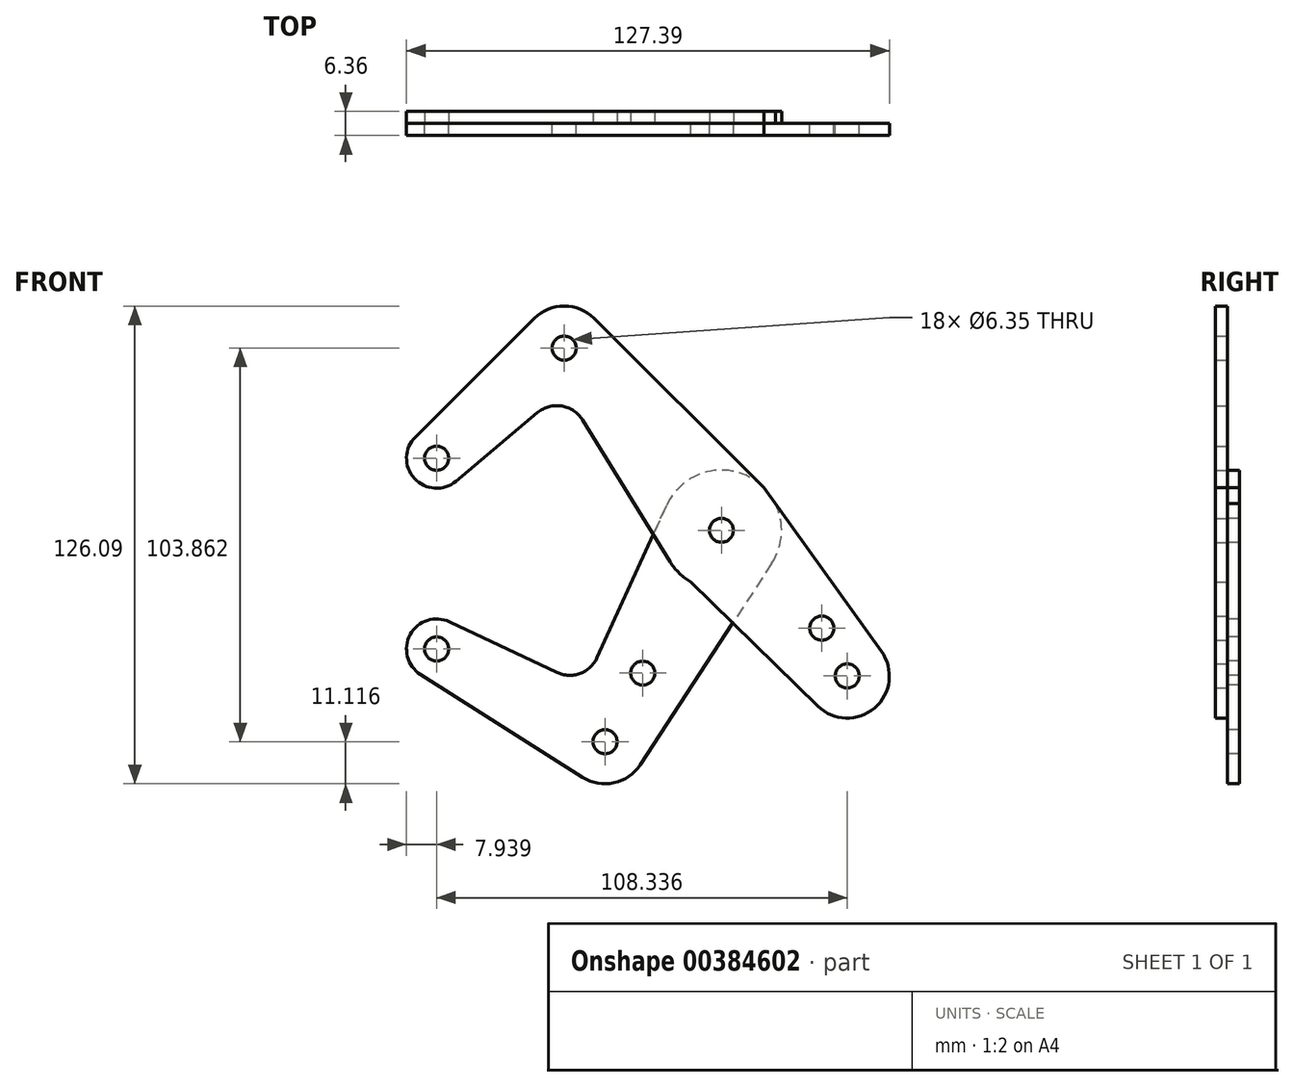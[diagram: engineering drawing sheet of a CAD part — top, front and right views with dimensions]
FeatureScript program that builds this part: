
annotation { "Feature Type Name" : "Feature", "Feature Type Description" : "" }
export const myFeature = defineFeature(function(context is Context, id is Id, definition is map)
    precondition{}
    {
        {
            var Q0;
            Q0=qCreatedBy(makeId("Front.planeOp"),FACE);
            var sketch = newSketch(context, id + "F0", { "sketchPlane" : qUnion([Q0])});
            skCircle(sketch, "E0", {"center": v(0, 0) * mm, "radius": 15.88 * mm});
            skCircle(sketch, "E1", {"center": v(-41.5, 48.07) * mm, "radius": 11.11 * mm});
            skCircle(sketch, "E2", {"center": v(33.2, -38.45) * mm, "radius": 11.11 * mm});
            skCircle(sketch, "E3", {"center": v(-75.14, 19.02) * mm, "radius": 7.94 * mm});
            skLineSegment(sketch, "E4", {"start": v(-80.74, 24.65) * mm, "end": v(-49.34, 55.94) * mm});
            skLineSegment(sketch, "E5", {"start": v(-33.65, 55.94) * mm, "end": v(11.2, 11.25) * mm});
            skLineSegment(sketch, "E6", {"start": v(11.2, 11.25) * mm, "end": v(42.22, -31.98) * mm});
            skLineSegment(sketch, "E7", {"start": v(-70.03, 12.95) * mm, "end": v(-48.54, 31.03) * mm});
            skLineSegment(sketch, "E8", {"start": v(-36.66, 29.13) * mm, "end": v(-13.5, -8.34) * mm});
            skLineSegment(sketch, "E9", {"start": v(-13.5, -8.34) * mm, "end": v(25.43, -46.4) * mm});
            skPoint(sketch, "E10.visualSharp", {"position": v(-41.5, 36.96) * mm});
            skArc(sketch, "E10.filletArc", {"start": v(-36.66, 29.13) * mm, "mid": v(-42.16, 32.8) * mm, "end": v(-48.54, 31.03) * mm});
            skCircle(sketch, "E11", {"center": v(33.2, -38.45) * mm, "radius": 3.18 * mm});
            skCircle(sketch, "E12", {"center": v(0, 0) * mm, "radius": 3.18 * mm});
            skCircle(sketch, "E13", {"center": v(-41.5, 48.07) * mm, "radius": 3.18 * mm});
            skCircle(sketch, "E14", {"center": v(-75.14, 19.02) * mm, "radius": 3.18 * mm});
            skLineSegment(sketch, "E15", {"start": v(-41.5, 48.07) * mm, "end": v(33.2, -38.45) * mm, "construction": true});
            skLineSegment(sketch, "E16", {"start": v(-75.14, 19.02) * mm, "end": v(-41.5, 48.07) * mm, "construction": true});
            skCircle(sketch, "E17", {"center": v(26.5, -25.83) * mm, "radius": 3.18 * mm});
            skCircle(sketch, "E18", {"center": v(0, 0) * mm, "radius": 3.98 * mm});
            skCircle(sketch, "E19", {"center": v(-30.7, -55.8) * mm, "radius": 11.11 * mm});
            skCircle(sketch, "E20", {"center": v(-20.74, -37.7) * mm, "radius": 3.18 * mm});
            skLineSegment(sketch, "E21", {"start": v(0, 0) * mm, "end": v(-30.7, -55.8) * mm, "construction": true});
            skLineSegment(sketch, "E22", {"start": v(13.3, -8.67) * mm, "end": v(-21.38, -61.86) * mm});
            skLineSegment(sketch, "E23", {"start": v(-32.8, -33.63) * mm, "end": v(-14.44, 6.59) * mm});
            skCircle(sketch, "E24", {"center": v(-75.14, -31.34) * mm, "radius": 7.94 * mm});
            skLineSegment(sketch, "E25", {"start": v(-75.14, 19.02) * mm, "end": v(-75.14, -31.34) * mm, "construction": true});
            skLineSegment(sketch, "E26", {"start": v(-71.76, -24.16) * mm, "end": v(-43.41, -37.52) * mm});
            skLineSegment(sketch, "E27", {"start": v(-79.4, -38.04) * mm, "end": v(-36.65, -65.18) * mm});
            skLineSegment(sketch, "E28", {"start": v(-75.14, -31.34) * mm, "end": v(-30.7, -55.8) * mm, "construction": true});
            skPoint(sketch, "E29.visualSharp", {"position": v(-36.13, -40.95) * mm});
            skArc(sketch, "E29.filletArc", {"start": v(-43.41, -37.52) * mm, "mid": v(-37.29, -37.79) * mm, "end": v(-32.8, -33.63) * mm});
            skCircle(sketch, "E30", {"center": v(-75.14, -31.34) * mm, "radius": 3.18 * mm});
            skCircle(sketch, "E31", {"center": v(-30.7, -55.8) * mm, "radius": 3.18 * mm});
            skSolve(sketch);
        }
        {
            var Q0;
            {var subQ0=sQuery(id+"F0.wireOp",EDGE,"E4");Q0=makeQuery(id+"F0.imprint","IMPRINT",FACE,{"disambiguationData":[TD([[makeQuery(id+"F0.imprint","IMPRINT",EDGE,{"derivedFrom":subQ0}),-1.0]])]});}
            var Q1;
            Q1=makeQuery(id+"F0.imprint","IMPRINT",FACE,{"disambiguationData":[TD([[makeQuery(id+"F0.imprint","IMPRINT",EDGE,{"derivedFrom":sQuery(id+"F0.wireOp",EDGE,"E18")}),-1.0]])]});
            var Q2;
            Q2=makeQuery(id+"F0.imprint","IMPRINT",FACE,{"disambiguationData":[TD([[makeQuery(id+"F0.imprint","IMPRINT",EDGE,{"derivedFrom":sQuery(id+"F0.wireOp",EDGE,"E13")}),-1.0]])]});
            var Q3;
            Q3=makeQuery(id+"F0.imprint","IMPRINT",FACE,{"disambiguationData":[TD([[makeQuery(id+"F0.imprint","IMPRINT",EDGE,{"derivedFrom":sQuery(id+"F0.wireOp",EDGE,"E14")}),-1.0]])]});
            var Q4;
            Q4=makeQuery(id+"F0.imprint","IMPRINT",FACE,{"disambiguationData":[TD([[makeQuery(id+"F0.imprint","IMPRINT",EDGE,{"derivedFrom":sQuery(id+"F0.wireOp",EDGE,"E12")}),-1.0]])]});
            var Q5;
            {var subQ1=sQuery(id+"F0.wireOp",EDGE,"E0");var subQ3=sQuery(id+"F0.wireOp",EDGE,"E23");var subQ4=makeQuery(id+"F0.imprint","INTERSECT",VERTEX,{"derivedFrom":[subQ1,subQ3]});Q5=makeQuery(id+"F0.imprint","IMPRINT",FACE,{"disambiguationData":[TD([[makeQuery(id+"F0.imprint","IMPRINT",EDGE,{"disambiguationData":[TD([[subQ4,1.0]])],"derivedFrom":subQ3}),-1.0]])]});}
            var Q6;
            {var subQ0=sQuery(id+"F0.wireOp",EDGE,"E22");var subQ1=sQuery(id+"F0.wireOp",EDGE,"E0");var subQ2=makeQuery(id+"F0.imprint","INTERSECT",VERTEX,{"derivedFrom":[subQ1,subQ0]});Q6=makeQuery(id+"F0.imprint","IMPRINT",FACE,{"disambiguationData":[TD([[makeQuery(id+"F0.imprint","IMPRINT",EDGE,{"disambiguationData":[TD([[subQ2,1.0]])],"derivedFrom":subQ1}),-1.0]])]});}
            var Q7;
            {var subQ9=sQuery(id+"F0.wireOp",EDGE,"E17");Q7=makeQuery(id+"F0.imprint","IMPRINT",FACE,{"disambiguationData":[TD([[makeQuery(id+"F0.imprint","IMPRINT",EDGE,{"derivedFrom":subQ9}),-1.0]])]});}
            var Q8;
            Q8=makeQuery(id+"F0.imprint","IMPRINT",FACE,{"disambiguationData":[TD([[makeQuery(id+"F0.imprint","IMPRINT",EDGE,{"derivedFrom":sQuery(id+"F0.wireOp",EDGE,"E11")}),-1.0]])]});
            var Q9;
            {var subQ0=sQuery(id+"F0.wireOp",EDGE,"E9");var subQ1=sQuery(id+"F0.wireOp",EDGE,"E0");var subQ3=makeQuery(id+"F0.imprint","INTERSECT",VERTEX,{"derivedFrom":[subQ1,subQ0]});Q9=makeQuery(id+"F0.imprint","IMPRINT",FACE,{"disambiguationData":[TD([[makeQuery(id+"F0.imprint","IMPRINT",EDGE,{"disambiguationData":[TD([[subQ3,1.0]])],"derivedFrom":subQ1}),1.0]])]});}
            extrude(context, id + "F1", {"entities" : qUnion([Q0, Q1, Q2, Q3, Q4, Q5, Q6, Q7, Q8, Q9]), "depth" : 3.17 * mm});
        }
        {
            var Q0;
            Q0=makeQuery(id+"F0.imprint","IMPRINT",FACE,{"disambiguationData":[TD([[makeQuery(id+"F0.imprint","IMPRINT",EDGE,{"derivedFrom":sQuery(id+"F0.wireOp",EDGE,"E20")}),-1.0]])]});
            var Q1;
            {var subQ0=sQuery(id+"F0.wireOp",EDGE,"E22");var subQ1=sQuery(id+"F0.wireOp",EDGE,"E0");var subQ2=makeQuery(id+"F0.imprint","INTERSECT",VERTEX,{"derivedFrom":[subQ1,subQ0]});Q1=makeQuery(id+"F0.imprint","IMPRINT",FACE,{"disambiguationData":[TD([[makeQuery(id+"F0.imprint","IMPRINT",EDGE,{"disambiguationData":[TD([[subQ2,1.0]])],"derivedFrom":subQ1}),-1.0]])]});}
            var Q2;
            Q2=makeQuery(id+"F0.imprint","IMPRINT",FACE,{"disambiguationData":[TD([[makeQuery(id+"F0.imprint","IMPRINT",EDGE,{"derivedFrom":sQuery(id+"F0.wireOp",EDGE,"E18")}),-1.0]])]});
            var Q3;
            Q3=makeQuery(id+"F0.imprint","IMPRINT",FACE,{"disambiguationData":[TD([[makeQuery(id+"F0.imprint","IMPRINT",EDGE,{"derivedFrom":sQuery(id+"F0.wireOp",EDGE,"E31")}),-1.0]])]});
            var Q4;
            Q4=makeQuery(id+"F0.imprint","IMPRINT",FACE,{"disambiguationData":[TD([[makeQuery(id+"F0.imprint","IMPRINT",EDGE,{"derivedFrom":sQuery(id+"F0.wireOp",EDGE,"E30")}),-1.0]])]});
            var Q5;
            {var subQ1=sQuery(id+"F0.wireOp",EDGE,"E0");var subQ3=sQuery(id+"F0.wireOp",EDGE,"E23");var subQ4=makeQuery(id+"F0.imprint","INTERSECT",VERTEX,{"derivedFrom":[subQ1,subQ3]});Q5=makeQuery(id+"F0.imprint","IMPRINT",FACE,{"disambiguationData":[TD([[makeQuery(id+"F0.imprint","IMPRINT",EDGE,{"disambiguationData":[TD([[subQ4,1.0]])],"derivedFrom":subQ3}),-1.0]])]});}
            var Q6;
            {var subQ0=sQuery(id+"F0.wireOp",EDGE,"E9");var subQ1=sQuery(id+"F0.wireOp",EDGE,"E0");var subQ3=makeQuery(id+"F0.imprint","INTERSECT",VERTEX,{"derivedFrom":[subQ1,subQ0]});Q6=makeQuery(id+"F0.imprint","IMPRINT",FACE,{"disambiguationData":[TD([[makeQuery(id+"F0.imprint","IMPRINT",EDGE,{"disambiguationData":[TD([[subQ3,1.0]])],"derivedFrom":subQ1}),1.0]])]});}
            var Q7;
            Q7=makeQuery(id+"F0.imprint","IMPRINT",FACE,{"disambiguationData":[TD([[makeQuery(id+"F0.imprint","IMPRINT",EDGE,{"derivedFrom":sQuery(id+"F0.wireOp",EDGE,"E12")}),-1.0]])]});
            extrude(context, id + "F2", {"entities" : qUnion([Q0, Q1, Q2, Q3, Q4, Q5, Q6, Q7]), "oppositeDirection" : true, "depth" : 3.17 * mm});
        }
    });
